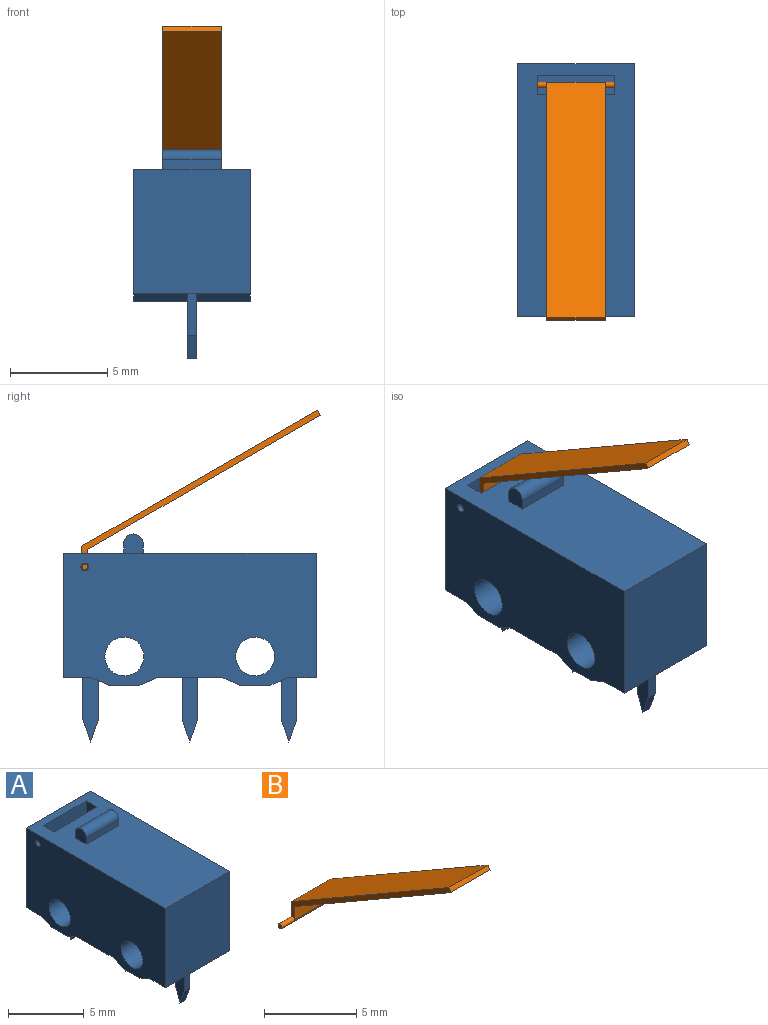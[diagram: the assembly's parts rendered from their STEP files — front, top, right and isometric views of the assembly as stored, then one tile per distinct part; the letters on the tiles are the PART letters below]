
ASSEMBLY  parts=2 mates=1
PART A: 46 faces, bbox 6x13x10.7 mm
  f0: plane 13x6mm, normal (0,0,1), area 71mm2, adj f5,f6,f16,f17,f36,f37,f38,f39
  f1: cylinder r=0.2mm len=1mm, axis (-1,0,0), area 1.3mm2, adj f16,f37
  f2: plane 6x1.47mm, normal (0,0,-1), area 8.6mm2, adj f6,f7,f16,f17,f19,f20,f21
  f3: plane 6x0.92mm, normal (0,0.4,-0.92), area 5.8mm2, adj f4,f13,f16,f17,f30,f34,f35
  f4: plane 6x1.47mm, normal (0,0,-1), area 8.6mm2, adj f3,f5,f16,f17,f33,f34,f35
  f5: plane 6.4x6mm, normal (0,1,0), area 38.4mm2, adj f0,f4,f16,f17
  f6: plane 6.4x6mm, normal (0,-1,0), area 38.4mm2, adj f0,f2,f16,f17
  f7: plane 6x0.92mm, normal (0,-0.4,-0.92), area 5.8mm2, adj f2,f8,f16,f17,f18,f19,f20
  f8: plane 6x1.5mm, normal (0,0,-1), area 9mm2, adj f7,f9,f16,f17
  f9: plane 6x0.92mm, normal (0,0.4,-0.92), area 6mm2, adj f8,f10,f16,f17
  f10: plane 6x3.4mm, normal (0,0,-1), area 20mm2, adj f9,f11,f16,f17,f24,f27,f28,f29
  f11: plane 6x0.92mm, normal (0,-0.4,-0.92), area 6mm2, adj f10,f13,f16,f17
  f12: cylinder r=1mm len=6mm, axis (-1,0,0), area 37.7mm2, adj f16,f17
  f13: plane 6x1.5mm, normal (0,0,-1), area 9mm2, adj f3,f11,f16,f17
  f14: cylinder r=0.2mm len=1mm, axis (-1,0,0), area 1.3mm2, adj f17,f39
  f15: cylinder r=1mm len=6mm, axis (-1,0,0), area 37.7mm2, adj f16,f17
  f16: plane 13x6.8mm, normal (1,0,0), area 78.7mm2, adj f0,f1,f2,f3,f4,f5,f6,f7
  f17: plane 13x6.8mm, normal (-1,0,0), area 78.7mm2, adj f0,f2,f3,f4,f5,f6,f7,f8
  f18: plane 2.02x0.5mm, normal (0,1,0), area 1mm2, adj f7,f19,f20,f23
  f19: plane 3.3x0.8mm, normal (1,0,0), area 2.2mm2, adj f2,f7,f18,f21,f22,f23
  f20: plane 3.3x0.8mm, normal (-1,0,0), area 2.2mm2, adj f2,f7,f18,f21,f22,f23
  f21: plane 2.17x0.5mm, normal (0,-1,0), area 1.1mm2, adj f2,f19,f20,f22
  f22: plane 1.13x0.5mm, normal (0,-0.94,-0.33), area 0.6mm2, adj f19,f20,f21,f23
  f23: plane 1.13x0.5mm, normal (0,0.94,-0.33), area 0.6mm2, adj f18,f19,f20,f22
  f24: plane 2.17x0.5mm, normal (0,-1,0), area 1.1mm2, adj f10,f25,f28,f29
  f25: plane 1.13x0.5mm, normal (0,-0.94,-0.33), area 0.6mm2, adj f24,f26,f28,f29
  f26: plane 1.13x0.5mm, normal (0,0.94,-0.33), area 0.6mm2, adj f25,f27,f28,f29
  f27: plane 2.17x0.5mm, normal (0,1,0), area 1.1mm2, adj f10,f26,f28,f29
  f28: plane 3.3x0.8mm, normal (1,0,0), area 2.2mm2, adj f10,f24,f25,f26,f27
  f29: plane 3.3x0.8mm, normal (-1,0,0), area 2.2mm2, adj f10,f24,f25,f26,f27
  f30: plane 2.02x0.5mm, normal (0,-1,0), area 1mm2, adj f3,f31,f34,f35
  f31: plane 1.13x0.5mm, normal (0,-0.94,-0.33), area 0.6mm2, adj f30,f32,f34,f35
  f32: plane 1.13x0.5mm, normal (0,0.94,-0.33), area 0.6mm2, adj f31,f33,f34,f35
  f33: plane 2.17x0.5mm, normal (0,1,0), area 1.1mm2, adj f4,f32,f34,f35
  f34: plane 3.3x0.8mm, normal (1,0,0), area 2.2mm2, adj f3,f4,f30,f31,f32,f33
  f35: plane 3.3x0.8mm, normal (-1,0,0), area 2.2mm2, adj f3,f4,f30,f31,f32,f33
  f36: plane 4x2mm, normal (0,1,0), area 8mm2, adj f0,f37,f39,f40
  f37: plane 2x1mm, normal (-1,0,0), area 1.9mm2, adj f0,f1,f36,f38,f40
  f38: plane 4x2mm, normal (0,-1,0), area 8mm2, adj f0,f37,f39,f40
  f39: plane 2x1mm, normal (1,0,0), area 1.9mm2, adj f0,f14,f36,f38,f40
  f40: plane 4x1mm, normal (0,0,1), area 4mm2, adj f36,f37,f38,f39
  f41: plane 3x0.5mm, normal (0,-1,0), area 1.5mm2, adj f0,f42,f44,f45
  f42: plane 1x1mm, normal (1,0,0), area 0.9mm2, adj f0,f41,f43,f45
  f43: plane 3x0.5mm, normal (0,1,0), area 1.5mm2, adj f0,f42,f44,f45
  f44: plane 1x1mm, normal (-1,0,0), area 0.9mm2, adj f0,f41,f43,f45
  f45: cylinder r=0.5mm len=3mm, axis (-1,0,0), area 4.7mm2, adj f41,f42,f43,f44
PART B: 10 faces, bbox 5x12.3x8.2 mm
  f0: plane 3x1.07mm, normal (0,1,0), area 3.2mm2, adj f1,f5,f6,f7
  f1: plane 12.12x7mm, normal (0,0.5,0.87), area 42mm2, adj f0,f2,f5,f6
  f2: plane 3x0.26mm, normal (0,-0.87,0.5), area 0.9mm2, adj f1,f3,f5,f6
  f3: plane 11.97x6.91mm, normal (0,-0.5,-0.87), area 41.5mm2, adj f2,f4,f5,f6
  f4: plane 3x0.9mm, normal (0,-1,0), area 2.7mm2, adj f3,f5,f6,f7
  f5: plane 12.27x8.07mm, normal (1,0,0), area 4.4mm2, adj f0,f1,f2,f3,f4,f7
  f6: plane 12.27x8.07mm, normal (-1,0,0), area 4.4mm2, adj f0,f1,f2,f3,f4,f7
  f7: cylinder r=0.15mm len=5mm, axis (-1,0,0), area 3.3mm2, adj f0,f4,f5,f6,f8,f9
  f8: plane 0.3x0.3mm, normal (1,0,0), area 0.1mm2, adj f7
  f9: plane 0.3x0.3mm, normal (-1,0,0), area 0.1mm2, adj f7
PLACE A t=(-3.97,-3.6,1.35)mm fixed
PLACE B t=(-3.97,-3.6,1.35)mm
MATE revolute A.f1 <-> B.f7  axis (-1,0,0) through (-1.47,1.8,3.85)mm
